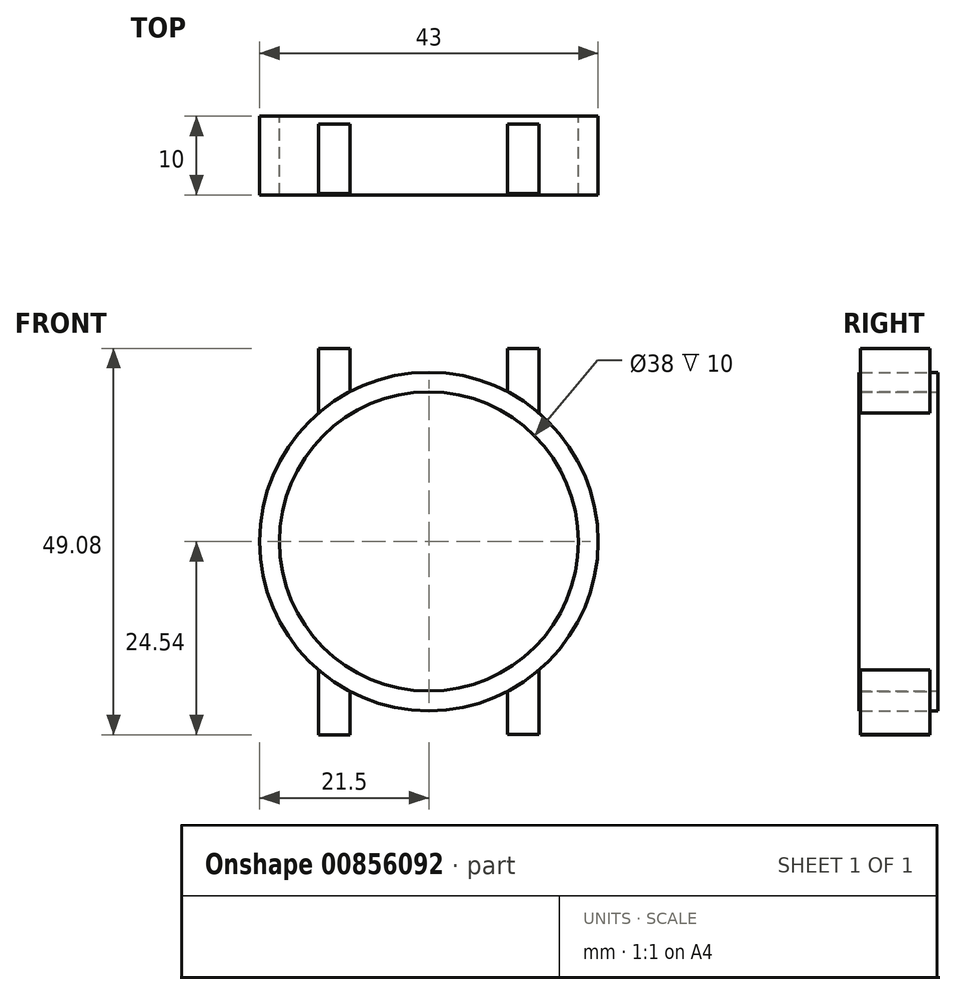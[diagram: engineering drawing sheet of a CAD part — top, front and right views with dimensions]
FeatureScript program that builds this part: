
annotation { "Feature Type Name" : "Feature", "Feature Type Description" : "" }
export const myFeature = defineFeature(function(context is Context, id is Id, definition is map)
    precondition{}
    {
        {
            var Q0;
            Q0=qCreatedBy(makeId("Front.planeOp"),FACE);
            var sketch = newSketch(context, id + "F0", { "sketchPlane" : qUnion([Q0])});
            skCircle(sketch, "E0", {"center": v(0, 0) * mm, "radius": 21.5 * mm});
            skLineSegment(sketch, "E1.bottom", {"start": v(-10, 19.04) * mm, "end": v(-14, 19.04) * mm});
            skLineSegment(sketch, "E1.top", {"start": v(-10, 24.54) * mm, "end": v(-14, 24.54) * mm});
            skLineSegment(sketch, "E1.left", {"start": v(-10, 19.04) * mm, "end": v(-10, 24.54) * mm});
            skLineSegment(sketch, "E1.right", {"start": v(-14, 19.04) * mm, "end": v(-14, 24.54) * mm});
            skLineSegment(sketch, "E2.bottom", {"start": v(10, 19.03) * mm, "end": v(14, 19.03) * mm});
            skLineSegment(sketch, "E2.top", {"start": v(10, 24.53) * mm, "end": v(14, 24.53) * mm});
            skLineSegment(sketch, "E2.left", {"start": v(10, 19.03) * mm, "end": v(10, 24.53) * mm});
            skLineSegment(sketch, "E2.right", {"start": v(14, 19.03) * mm, "end": v(14, 24.53) * mm});
            skLineSegment(sketch, "E3", {"start": v(-14, 19.04) * mm, "end": v(-14, 16.32) * mm});
            skLineSegment(sketch, "E4", {"start": v(14, 19.03) * mm, "end": v(14, 16.3) * mm});
            skCircle(sketch, "E5", {"center": v(0, 0) * mm, "radius": 19 * mm});
            skCircle(sketch, "E6", {"center": v(0, 0) * mm, "radius": 21 * mm});
            skPoint(sketch, "E7", {"position": v(-16.4, -11) * mm});
            skPoint(sketch, "E8", {"position": v(16.4, -11) * mm});
            skPoint(sketch, "E9", {"position": v(0, -19.75) * mm});
            skLineSegment(sketch, "E10", {"start": v(-33.8, 0) * mm, "end": v(39.15, 0) * mm, "construction": true});
            skPoint(sketch, "E11.MirrorP", {"position": v(-16.4, 11) * mm});
            skPoint(sketch, "E12.MirrorP", {"position": v(0, 19.75) * mm});
            skPoint(sketch, "E13.MirrorP", {"position": v(16.4, 11) * mm});
            skLineSegment(sketch, "E14.MirrorCS", {"start": v(14, -19.03) * mm, "end": v(14, -16.3) * mm});
            skLineSegment(sketch, "E15.MirrorCS", {"start": v(-14, -19.04) * mm, "end": v(-14, -16.32) * mm});
            skLineSegment(sketch, "E16.MirrorCS", {"start": v(-10, -19.04) * mm, "end": v(-10, -24.54) * mm});
            skLineSegment(sketch, "E17.MirrorCS", {"start": v(-14, -19.04) * mm, "end": v(-14, -24.54) * mm});
            skLineSegment(sketch, "E18.MirrorCS", {"start": v(-10, -19.04) * mm, "end": v(-14, -19.04) * mm});
            skLineSegment(sketch, "E19.MirrorCS", {"start": v(10, -19.03) * mm, "end": v(14, -19.03) * mm});
            skLineSegment(sketch, "E20.MirrorCS", {"start": v(14, -19.03) * mm, "end": v(14, -24.53) * mm});
            skLineSegment(sketch, "E21.MirrorCS", {"start": v(-10, -24.54) * mm, "end": v(-14, -24.54) * mm});
            skLineSegment(sketch, "E22.MirrorCS", {"start": v(10, -19.03) * mm, "end": v(10, -24.53) * mm});
            skLineSegment(sketch, "E23.MirrorCS", {"start": v(10, -24.53) * mm, "end": v(14, -24.53) * mm});
            skSolve(sketch);
        }
        {
            var Q0;
            Q0=makeQuery(id+"F0.imprint","IMPRINT",FACE,{"disambiguationData":[TD([[makeQuery(id+"F0.imprint","IMPRINT",EDGE,{"derivedFrom":sQuery(id+"F0.wireOp",EDGE,"E6")}),-1.0]])]});
            var Q1;
            Q1=makeQuery(id+"F0.imprint","IMPRINT",FACE,{"disambiguationData":[TD([[makeQuery(id+"F0.imprint","IMPRINT",EDGE,{"derivedFrom":sQuery(id+"F0.wireOp",EDGE,"E5")}),-1.0]])]});
            extrude(context, id + "F1", {"entities" : qUnion([Q0, Q1]), "depth" : 10 * mm, "offsetDistance" : 25 * mm});
        }
        {
            var Q0;
            Q0=makeQuery(id+"F0.imprint","IMPRINT",FACE,{"disambiguationData":[TD([[makeQuery(id+"F0.imprint","IMPRINT",EDGE,{"derivedFrom":sQuery(id+"F0.wireOp",EDGE,"E2.bottom")}),1.0]])]});
            var Q1;
            {var subQ0=sQuery(id+"F0.wireOp",EDGE,"E2.bottom");Q1=makeQuery(id+"F0.imprint","IMPRINT",FACE,{"disambiguationData":[TD([[makeQuery(id+"F0.imprint","IMPRINT",EDGE,{"derivedFrom":subQ0}),-1.0]])]});}
            var Q2;
            Q2=makeQuery(id+"F0.imprint","IMPRINT",FACE,{"disambiguationData":[TD([[makeQuery(id+"F0.imprint","IMPRINT",EDGE,{"derivedFrom":sQuery(id+"F0.wireOp",EDGE,"E1.bottom")}),-1.0]])]});
            var Q3;
            {var subQ0=sQuery(id+"F0.wireOp",EDGE,"E1.bottom");Q3=makeQuery(id+"F0.imprint","IMPRINT",FACE,{"disambiguationData":[TD([[makeQuery(id+"F0.imprint","IMPRINT",EDGE,{"derivedFrom":subQ0}),1.0]])]});}
            var Q4;
            Q4=makeQuery(id+"F0.imprint","IMPRINT",FACE,{"disambiguationData":[TD([[makeQuery(id+"F0.imprint","IMPRINT",EDGE,{"derivedFrom":sQuery(id+"F0.wireOp",EDGE,"E22.MirrorCS")}),1.0]])]});
            var Q5;
            Q5=makeQuery(id+"F0.imprint","IMPRINT",FACE,{"disambiguationData":[TD([[makeQuery(id+"F0.imprint","IMPRINT",EDGE,{"derivedFrom":sQuery(id+"F0.wireOp",EDGE,"E17.MirrorCS")}),1.0]])]});
            var Q6;
            {var subQ0=sQuery(id+"F0.wireOp",EDGE,"E15.MirrorCS");Q6=makeQuery(id+"F0.imprint","IMPRINT",FACE,{"disambiguationData":[TD([[makeQuery(id+"F0.imprint","IMPRINT",EDGE,{"derivedFrom":subQ0}),-1.0]])]});}
            var Q7;
            {var subQ0=sQuery(id+"F0.wireOp",EDGE,"E14.MirrorCS");Q7=makeQuery(id+"F0.imprint","IMPRINT",FACE,{"disambiguationData":[TD([[makeQuery(id+"F0.imprint","IMPRINT",EDGE,{"derivedFrom":subQ0}),1.0]])]});}
            extrude(context, id + "F2", {"entities" : qUnion([Q0, Q1, Q2, Q3, Q4, Q5, Q6, Q7]), "operationType" : NewBodyOperationType.ADD, "depth" : 9.8 * mm, "offsetDistance" : 25 * mm, "hasSecondDirection" : true, "secondDirectionOppositeDirection" : true, "secondDirectionDepth" : -1 * mm});
        }
    });
